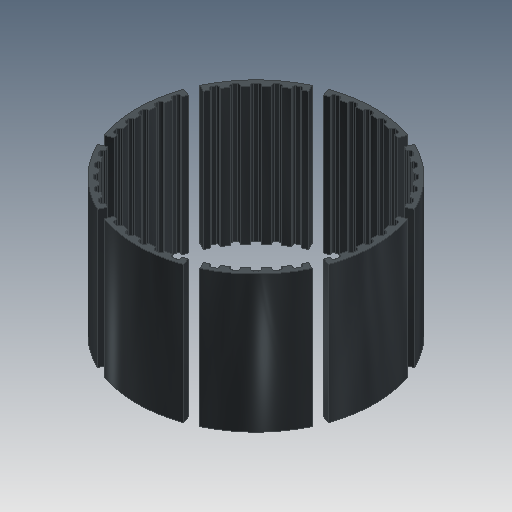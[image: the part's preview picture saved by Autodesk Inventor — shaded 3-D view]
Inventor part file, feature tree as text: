
AUTODESK INVENTOR PART (.ipt)
format: ipt  version: 2020.2 (Build 242310000, 310)  size: 427,008 bytes
history: native  units: mm
features: extrude x2, pattern_circular x2, sketch x2, fillet x1
ambient origin geometry x8: Origin, YZ Plane, XZ Plane, XY Plane, X Axis, Y Axis, Z Axis, Center Point
bodies: Body1 (feature_tree)
feature tree (7):
  extrude  "Extrusion7"  Depth=13.9mm
  extrude  "Extrusion8"  Depth=16.0mm TaperAngle=0.0deg
  pattern_circular  "Circular Pattern1"  [2 undecoded]
  fillet  "Fillet8"  Radius=6.806784mm
  pattern_circular  "Circular Pattern2"  [2 undecoded]
  sketch  "Sketch11"  dims[d82=13.0mm d83=13.9mm]
  sketch  "Sketch12"  dims[d84=80.0mm d86=360.0deg d89=16.0mm d90=0.0mm d91=6.806784mm d92=6.806784mm d94=0.9mm d95=16.0mm d96=0.0mm d97=50.0mm d98=30.0deg d100=0.25mm d101=80.0mm d102=360.0deg]
note: 4 required parameter values undecoded (feature->parameter linkage not recoverable at this tier; creation-order binding heuristic only, values carry confidence <= 0.55)
